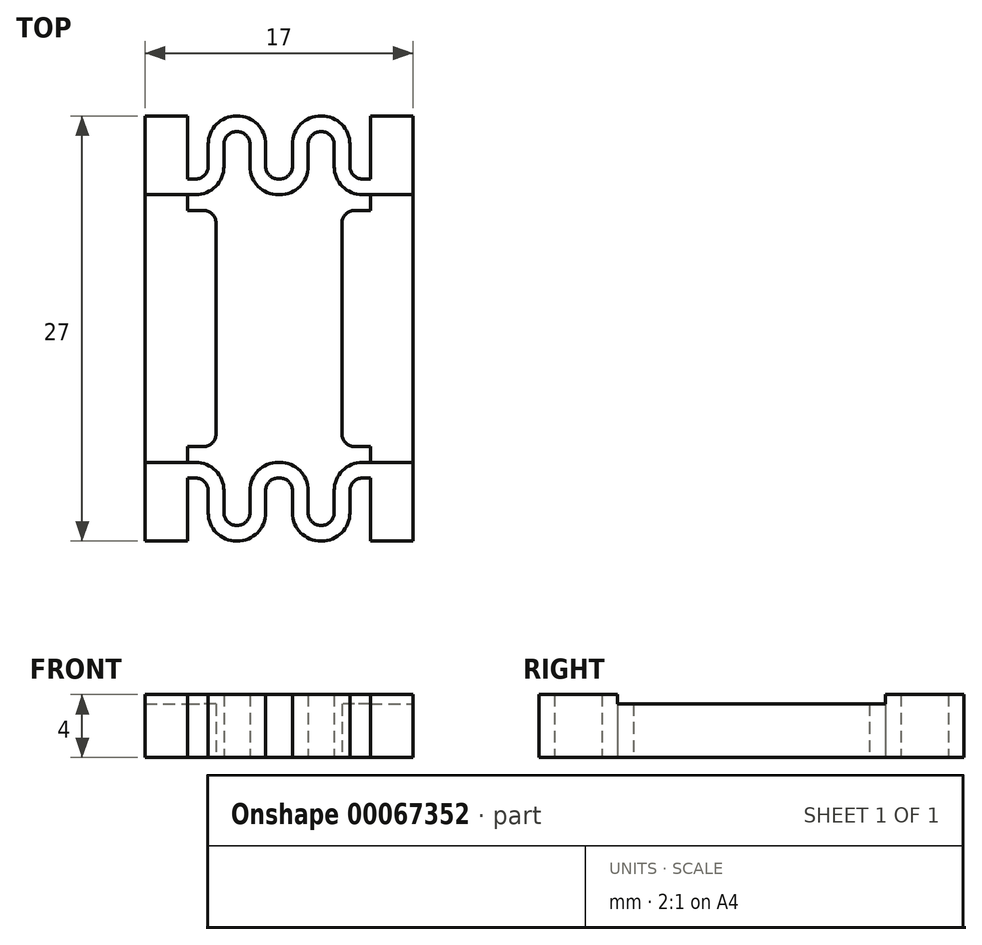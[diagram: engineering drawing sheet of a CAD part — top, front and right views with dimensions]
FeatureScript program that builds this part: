
annotation { "Feature Type Name" : "Feature", "Feature Type Description" : "" }
export const myFeature = defineFeature(function(context is Context, id is Id, definition is map)
    precondition{}
    {
        {
            var Q0;
            Q0=qCreatedBy(makeId("Top.planeOp"),FACE);
            var sketch = newSketch(context, id + "F0", { "sketchPlane" : qUnion([Q0])});
            skLineSegment(sketch, "E0", {"start": v(-4, 0) * mm, "end": v(-8.5, 0) * mm});
            skLineSegment(sketch, "E1", {"start": v(-8.5, 0) * mm, "end": v(-8.5, 13.5) * mm});
            skLineSegment(sketch, "E2", {"start": v(-8.5, 13.5) * mm, "end": v(-5.8, 13.5) * mm});
            skLineSegment(sketch, "E3", {"start": v(-0.85, 11.7) * mm, "end": v(-0.85, 10.3) * mm});
            skLineSegment(sketch, "E4", {"start": v(-0.05, 9.5) * mm, "end": v(0.05, 9.5) * mm});
            skLineSegment(sketch, "E5", {"start": v(0.85, 10.3) * mm, "end": v(0.85, 11.7) * mm});
            skLineSegment(sketch, "E6", {"start": v(2.65, 13.5) * mm, "end": v(2.7, 13.5) * mm});
            skLineSegment(sketch, "E7", {"start": v(8.5, 13.5) * mm, "end": v(8.5, 0) * mm});
            skLineSegment(sketch, "E8", {"start": v(8.5, 0) * mm, "end": v(4, 0) * mm});
            skLineSegment(sketch, "E9", {"start": v(3.5, 10.3) * mm, "end": v(3.5, 11.7) * mm});
            skLineSegment(sketch, "E10", {"start": v(2.7, 12.5) * mm, "end": v(2.65, 12.5) * mm});
            skLineSegment(sketch, "E11", {"start": v(1.85, 11.7) * mm, "end": v(1.85, 10.3) * mm});
            skLineSegment(sketch, "E12", {"start": v(0.05, 8.5) * mm, "end": v(-0.05, 8.5) * mm});
            skLineSegment(sketch, "E13", {"start": v(-1.85, 10.3) * mm, "end": v(-1.85, 11.7) * mm});
            skLineSegment(sketch, "E14", {"start": v(-2.65, 12.5) * mm, "end": v(-2.7, 12.5) * mm});
            skLineSegment(sketch, "E15", {"start": v(-3.5, 11.7) * mm, "end": v(-3.5, 10.3) * mm});
            skPoint(sketch, "E16.visualSharp", {"position": v(-3.5, 12.5) * mm});
            skArc(sketch, "E16.filletArc", {"start": v(-2.7, 12.5) * mm, "mid": v(-3.27, 12.27) * mm, "end": v(-3.5, 11.7) * mm});
            skPoint(sketch, "E17.visualSharp", {"position": v(-1.85, 12.5) * mm});
            skArc(sketch, "E17.filletArc", {"start": v(-1.85, 11.7) * mm, "mid": v(-2.08, 12.27) * mm, "end": v(-2.65, 12.5) * mm});
            skPoint(sketch, "E18.visualSharp", {"position": v(-0.85, 9.5) * mm});
            skArc(sketch, "E18.filletArc", {"start": v(-0.85, 10.3) * mm, "mid": v(-0.62, 9.73) * mm, "end": v(-0.05, 9.5) * mm});
            skPoint(sketch, "E19.visualSharp", {"position": v(0.85, 9.5) * mm});
            skArc(sketch, "E19.filletArc", {"start": v(0.05, 9.5) * mm, "mid": v(0.62, 9.73) * mm, "end": v(0.85, 10.3) * mm});
            skPoint(sketch, "E20.visualSharp", {"position": v(1.85, 12.5) * mm});
            skArc(sketch, "E20.filletArc", {"start": v(2.65, 12.5) * mm, "mid": v(2.08, 12.27) * mm, "end": v(1.85, 11.7) * mm});
            skPoint(sketch, "E21.visualSharp", {"position": v(3.5, 12.5) * mm});
            skArc(sketch, "E21.filletArc", {"start": v(3.5, 11.7) * mm, "mid": v(3.27, 12.27) * mm, "end": v(2.7, 12.5) * mm});
            skPoint(sketch, "E22.visualSharp", {"position": v(-0.85, 13.5) * mm});
            skArc(sketch, "E22.filletArc", {"start": v(-0.85, 11.7) * mm, "mid": v(-1.38, 12.97) * mm, "end": v(-2.65, 13.5) * mm});
            skPoint(sketch, "E23.visualSharp", {"position": v(0.85, 13.5) * mm});
            skArc(sketch, "E23.filletArc", {"start": v(2.65, 13.5) * mm, "mid": v(1.38, 12.97) * mm, "end": v(0.85, 11.7) * mm});
            skPoint(sketch, "E24.visualSharp", {"position": v(-1.85, 8.5) * mm});
            skArc(sketch, "E24.filletArc", {"start": v(-1.85, 10.3) * mm, "mid": v(-1.32, 9.03) * mm, "end": v(-0.05, 8.5) * mm});
            skPoint(sketch, "E25.visualSharp", {"position": v(1.85, 8.5) * mm});
            skArc(sketch, "E25.filletArc", {"start": v(0.05, 8.5) * mm, "mid": v(1.32, 9.03) * mm, "end": v(1.85, 10.3) * mm});
            skLineSegment(sketch, "E26", {"start": v(4.5, 11.7) * mm, "end": v(4.5, 10.3) * mm});
            skLineSegment(sketch, "E27", {"start": v(5.3, 9.5) * mm, "end": v(5.8, 9.5) * mm});
            skLineSegment(sketch, "E28", {"start": v(5.8, 9.5) * mm, "end": v(5.8, 13.5) * mm});
            skLineSegment(sketch, "E29.trimOffspring", {"start": v(5.8, 13.5) * mm, "end": v(8.5, 13.5) * mm});
            skLineSegment(sketch, "E30", {"start": v(-4.5, 11.7) * mm, "end": v(-4.5, 10.3) * mm});
            skLineSegment(sketch, "E31", {"start": v(-5.3, 9.5) * mm, "end": v(-5.8, 9.5) * mm});
            skLineSegment(sketch, "E32", {"start": v(-5.8, 9.5) * mm, "end": v(-5.8, 13.5) * mm});
            skLineSegment(sketch, "E33.trimOffspring", {"start": v(-2.7, 13.5) * mm, "end": v(-2.65, 13.5) * mm});
            skPoint(sketch, "E34.visualSharp", {"position": v(-4.5, 13.5) * mm});
            skArc(sketch, "E34.filletArc", {"start": v(-2.7, 13.5) * mm, "mid": v(-3.97, 12.97) * mm, "end": v(-4.5, 11.7) * mm});
            skPoint(sketch, "E35.visualSharp", {"position": v(4.5, 13.5) * mm});
            skArc(sketch, "E35.filletArc", {"start": v(4.5, 11.7) * mm, "mid": v(3.97, 12.97) * mm, "end": v(2.7, 13.5) * mm});
            skPoint(sketch, "E36.visualSharp", {"position": v(-4.5, 9.5) * mm});
            skArc(sketch, "E36.filletArc", {"start": v(-5.3, 9.5) * mm, "mid": v(-4.73, 9.73) * mm, "end": v(-4.5, 10.3) * mm});
            skPoint(sketch, "E37.visualSharp", {"position": v(4.5, 9.5) * mm});
            skArc(sketch, "E37.filletArc", {"start": v(4.5, 10.3) * mm, "mid": v(4.73, 9.73) * mm, "end": v(5.3, 9.5) * mm});
            skLineSegment(sketch, "E38", {"start": v(-4, 0) * mm, "end": v(-4, 6.7) * mm});
            skLineSegment(sketch, "E39", {"start": v(4, 0) * mm, "end": v(4, 6.7) * mm});
            skPoint(sketch, "E40.orphan", {"position": v(-3.5, 0) * mm});
            skPoint(sketch, "E41.orphan", {"position": v(3.5, 0) * mm});
            skLineSegment(sketch, "E42", {"start": v(-5.8, 7.5) * mm, "end": v(-4.8, 7.5) * mm});
            skPoint(sketch, "E43.visualSharp", {"position": v(-3.5, 8.5) * mm});
            skArc(sketch, "E43.filletArc", {"start": v(-5.3, 8.5) * mm, "mid": v(-4.03, 9.03) * mm, "end": v(-3.5, 10.3) * mm});
            skLineSegment(sketch, "E44", {"start": v(-5.3, 8.5) * mm, "end": v(-5.8, 8.5) * mm});
            skLineSegment(sketch, "E45", {"start": v(-5.8, 8.5) * mm, "end": v(-5.8, 7.5) * mm});
            skLineSegment(sketch, "E46", {"start": v(5.3, 8.5) * mm, "end": v(5.8, 8.5) * mm});
            skLineSegment(sketch, "E47", {"start": v(5.8, 8.5) * mm, "end": v(5.8, 7.5) * mm});
            skLineSegment(sketch, "E48", {"start": v(5.8, 7.5) * mm, "end": v(4.8, 7.5) * mm});
            skPoint(sketch, "E49.visualSharp", {"position": v(-4, 7.5) * mm});
            skArc(sketch, "E49.filletArc", {"start": v(-4, 6.7) * mm, "mid": v(-4.23, 7.27) * mm, "end": v(-4.8, 7.5) * mm});
            skPoint(sketch, "E50.visualSharp", {"position": v(4, 7.5) * mm});
            skArc(sketch, "E50.filletArc", {"start": v(4.8, 7.5) * mm, "mid": v(4.23, 7.27) * mm, "end": v(4, 6.7) * mm});
            skPoint(sketch, "E51.visualSharp", {"position": v(3.5, 8.5) * mm});
            skArc(sketch, "E51.filletArc", {"start": v(3.5, 10.3) * mm, "mid": v(4.03, 9.03) * mm, "end": v(5.3, 8.5) * mm});
            skSolve(sketch);
        }
        {
            var Q0;
            Q0 = qSketchRegion(id + "F0", true);
            extrude(context, id + "F1", {"entities" : qUnion([Q0]), "depth" : 4 * mm});
        }
        {
            var Q0;
            Q0=makeQuery(id+"F1.opExtrude","SWEPT_BODY",BODY,{"disambiguationData":[OSD([sQuery(id+"F0.wireOp",EDGE,"E0"),sQuery(id+"F0.wireOp",EDGE,"E1"),sQuery(id+"F0.wireOp",EDGE,"E2"),sQuery(id+"F0.wireOp",EDGE,"E3"),sQuery(id+"F0.wireOp",EDGE,"E4"),sQuery(id+"F0.wireOp",EDGE,"E5"),sQuery(id+"F0.wireOp",EDGE,"E6"),sQuery(id+"F0.wireOp",EDGE,"E7"),sQuery(id+"F0.wireOp",EDGE,"E8"),sQuery(id+"F0.wireOp",EDGE,"E9"),sQuery(id+"F0.wireOp",EDGE,"E10"),sQuery(id+"F0.wireOp",EDGE,"E11"),sQuery(id+"F0.wireOp",EDGE,"E12"),sQuery(id+"F0.wireOp",EDGE,"E13"),sQuery(id+"F0.wireOp",EDGE,"E14"),sQuery(id+"F0.wireOp",EDGE,"E15"),sQuery(id+"F0.wireOp",EDGE,"E16.filletArc"),sQuery(id+"F0.wireOp",EDGE,"E17.filletArc"),sQuery(id+"F0.wireOp",EDGE,"E18.filletArc"),sQuery(id+"F0.wireOp",EDGE,"E19.filletArc"),sQuery(id+"F0.wireOp",EDGE,"E20.filletArc"),sQuery(id+"F0.wireOp",EDGE,"E21.filletArc"),sQuery(id+"F0.wireOp",EDGE,"E22.filletArc"),sQuery(id+"F0.wireOp",EDGE,"E23.filletArc"),sQuery(id+"F0.wireOp",EDGE,"E24.filletArc"),sQuery(id+"F0.wireOp",EDGE,"E25.filletArc")])]});
            var Q1;
            Q1=qCreatedBy(makeId("Front.planeOp"),FACE);
            mirror(context, id + "F2", {"operationType" : NewBodyOperationType.ADD, "entities" : qUnion([Q0]), "mirrorPlane" : qUnion([Q1])});
        }
        {
            var Q0;
            {var subQ0=makeQuery(id+"F1.opExtrude","CAP_FACE",FACE,{"disambiguationData":[OSD([sQuery(id+"F0.wireOp",EDGE,"E0"),sQuery(id+"F0.wireOp",EDGE,"E1"),sQuery(id+"F0.wireOp",EDGE,"E2"),sQuery(id+"F0.wireOp",EDGE,"E3"),sQuery(id+"F0.wireOp",EDGE,"E4"),sQuery(id+"F0.wireOp",EDGE,"E5"),sQuery(id+"F0.wireOp",EDGE,"E6"),sQuery(id+"F0.wireOp",EDGE,"E7"),sQuery(id+"F0.wireOp",EDGE,"E8"),sQuery(id+"F0.wireOp",EDGE,"E9"),sQuery(id+"F0.wireOp",EDGE,"E10"),sQuery(id+"F0.wireOp",EDGE,"E11"),sQuery(id+"F0.wireOp",EDGE,"E12"),sQuery(id+"F0.wireOp",EDGE,"E13"),sQuery(id+"F0.wireOp",EDGE,"E14"),sQuery(id+"F0.wireOp",EDGE,"E15"),sQuery(id+"F0.wireOp",EDGE,"E16.filletArc"),sQuery(id+"F0.wireOp",EDGE,"E17.filletArc"),sQuery(id+"F0.wireOp",EDGE,"E18.filletArc"),sQuery(id+"F0.wireOp",EDGE,"E19.filletArc"),sQuery(id+"F0.wireOp",EDGE,"E20.filletArc"),sQuery(id+"F0.wireOp",EDGE,"E21.filletArc"),sQuery(id+"F0.wireOp",EDGE,"E22.filletArc"),sQuery(id+"F0.wireOp",EDGE,"E23.filletArc"),sQuery(id+"F0.wireOp",EDGE,"E24.filletArc"),sQuery(id+"F0.wireOp",EDGE,"E25.filletArc")])],"isStart":false});Q0=makeQuery(id+"F2.boolean.opBoolean","MERGE",FACE,{"derivedFrom":[subQ0,makeQuery(id+"F2.opPattern","COPY",FACE,{"derivedFrom":subQ0,"instanceName":"1"})]});}
            var sketch = newSketch(context, id + "F3", { "sketchPlane" : qUnion([Q0])});
            skLineSegment(sketch, "E52.bottom", {"start": v(-8.5, 8.5) * mm, "end": v(8.5, 8.5) * mm});
            skLineSegment(sketch, "E52.top", {"start": v(-8.5, -8.5) * mm, "end": v(8.5, -8.5) * mm});
            skLineSegment(sketch, "E52.left", {"start": v(-8.5, 8.5) * mm, "end": v(-8.5, -8.5) * mm});
            skLineSegment(sketch, "E52.right", {"start": v(8.5, 8.5) * mm, "end": v(8.5, -8.5) * mm});
            skSolve(sketch);
        }
        {
            var Q0;
            Q0 = qSketchRegion(id + "F3", true);
            extrude(context, id + "F4", {"entities" : qUnion([Q0]), "operationType" : NewBodyOperationType.REMOVE, "oppositeDirection" : true, "depth" : 0.6 * mm});
        }
    });
